# Revit family: BE_24111_en_GB
name_source: partatom
category: Leuchten
units: mm (PartAtom-declared; Revit-internal decimal feet)

## family parameters
Basisbauteil = Fläche
Beim Laden mit Abzugskörper schneiden = Ja
Bemaßung runder Anschluss = Durchmesser verwenden
Gemeinsam genutzt = Nein
Lichtquelle = Ja
Raumberechnungspunkt = Ja
Teiletyp = Normal

## types (4) — shared parameters
AC/DC = AC/DC
Ambient_temperature = 25 °C
BEGA_dummy = Nein
BEGA_internal = Ja
BEGA_internal_off = Ja
BEGA_internal_on = Ja
BEGA_internal_structure = Ja
Bega_IES = Ja
Beschreibung = Recessed wall luminaire
CE_conformity = yes
Colour_rendering_index = CRI > 80
Custom_made_product = Nein
Description_custom_made_product = Here you can specify modifications of your custom-made product
ENEC = yes
Energy_efficiency_class = LED A++ - A
Farbfilter = 16777215
Farbtemperaturverschiebung bei Dämpfen der Lampe = <Keine Auswahl>
Frequency = 0/50-60 Hz
Hersteller = BEGA
Installation_housing = Nein
Lampe = LED 8.9 W
Load_Classification = Lighting
Logo = BEGA_Logo.png
Material_02 = BEGA_finishes_silver_matt
Material_06 = BEGA_finishes_stainless_steel_brushed
Material_10 = BEGA_glass_matt
Neigungswinkel = 0,00°
Order_number_installation_housing = ---
Product_data_sheet = https://cdn.bega.com
Protection_class = IP 65
Recessed_depth = 110 mm
Recessed_opening = 175 mm
Safety_class = I
Scheinlast = 0 VA
Service_life_criteria = L70B50 @ 25 °C = 175000 h
Typenbild = 24111.png
URL = https://www.bega.com
Update = 2022-05-18T04:00:13
Voltage = 240 V
Weight = 1.3 kg
zero-valued in all types: Vorgabe-Ansicht

## per-type parameters (varying)
| type | Colour_temperature | Datei für fotometrisches Netz | LED_module_designation | Lamp_luminous_flux | Luminaire_luminous_flux | M_A | M_G | Modell | Order_number |
| BEGA_24111_silver_K4 | 4000 K | BE_24111K4.IES | LED-0621/840 | 1505 lm | 967 lm | Ja | Nein | 24111AK4 | 24111AK4 |
| BEGA_24111_silver_K3 | 3000 K | BE_24111.IES | LED-0621/830 | 1480 lm | 951 lm | Ja | Nein | 24111A | 24111AK3 |
| BEGA_24111_graphite_K3 | 3000 K | BE_24111K4.IES | LED-0621/830 | 1480 lm | 951 lm | Nein | Ja | 24111AK4 | 24111K3 |
| BEGA_24111_graphite_K4 | 4000 K | BE_24111K4.IES | LED-0621/840 | 1505 lm | 967 lm | Nein | Ja | 24111AK4 | 24111K4 |

## geometry (parser evidence)
native form markers: Sweep x2
no freeform markers — native parametric forms only
